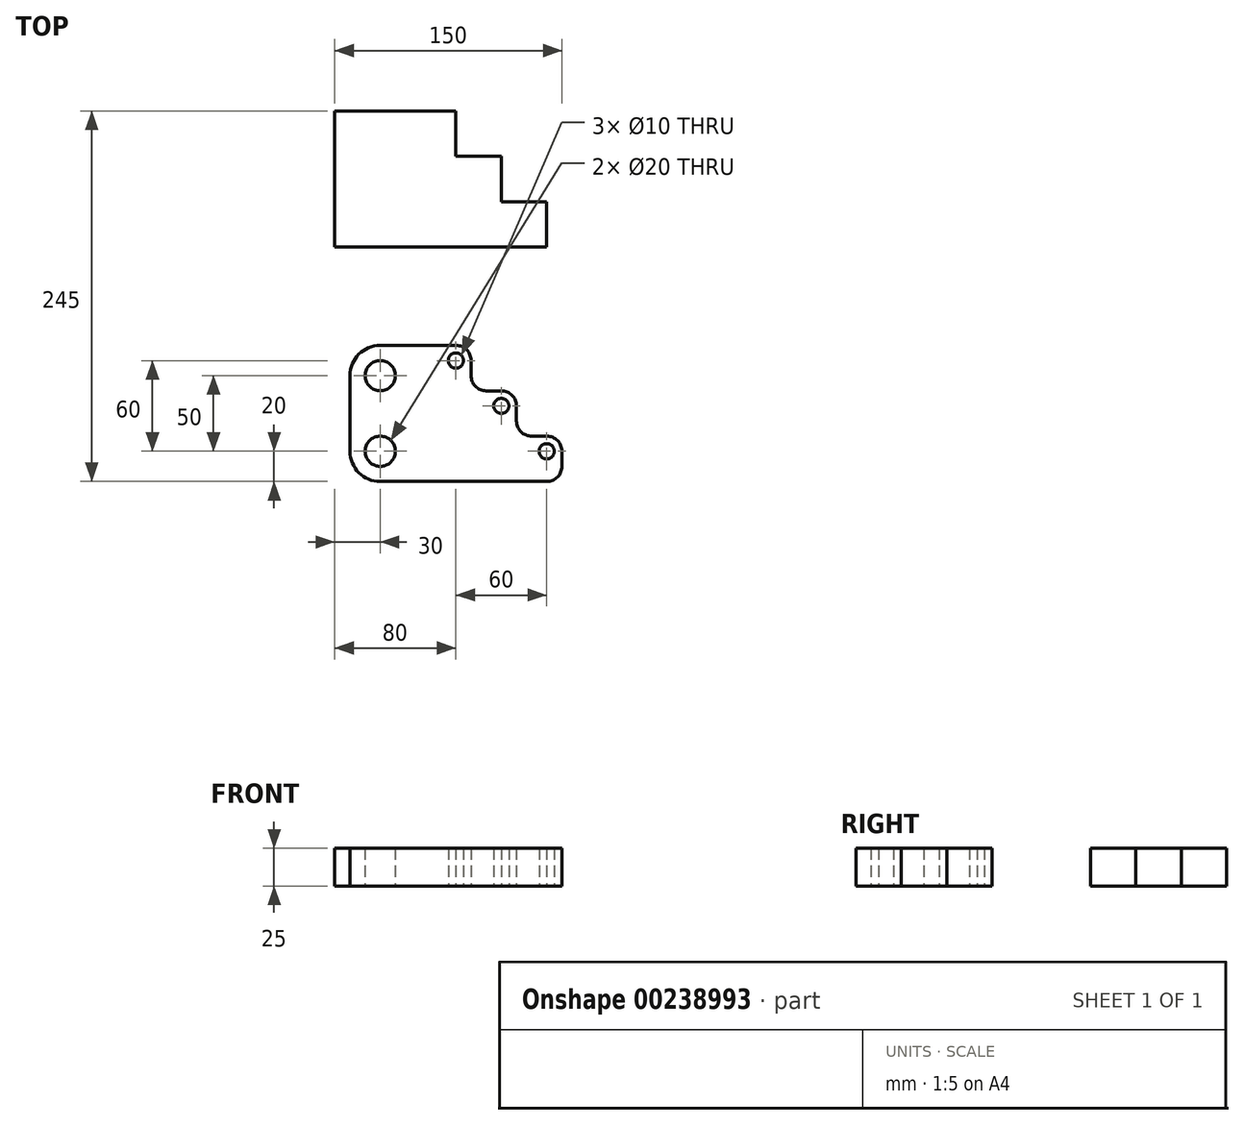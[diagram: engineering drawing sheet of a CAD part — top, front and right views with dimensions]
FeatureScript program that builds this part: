
annotation { "Feature Type Name" : "Feature", "Feature Type Description" : "" }
export const myFeature = defineFeature(function(context is Context, id is Id, definition is map)
    precondition{}
    {
        {
            var Q0;
            Q0=qCreatedBy(makeId("Top.planeOp"),FACE);
            var sketch = newSketch(context, id + "F0", { "sketchPlane" : qUnion([Q0])});
            skLineSegment(sketch, "E0", {"start": v(-110, 89.86) * mm, "end": v(-110, -0.14) * mm});
            skLineSegment(sketch, "E1", {"start": v(-110, 89.86) * mm, "end": v(-30, 89.86) * mm});
            skLineSegment(sketch, "E2", {"start": v(-30, 89.86) * mm, "end": v(-30, 59.86) * mm});
            skLineSegment(sketch, "E3", {"start": v(-30, 59.86) * mm, "end": v(0, 59.86) * mm});
            skLineSegment(sketch, "E4", {"start": v(0, 59.86) * mm, "end": v(0, 29.86) * mm});
            skLineSegment(sketch, "E5", {"start": v(0, 29.86) * mm, "end": v(30, 29.86) * mm});
            skLineSegment(sketch, "E6", {"start": v(30, 29.86) * mm, "end": v(30, -0.14) * mm});
            skLineSegment(sketch, "E7", {"start": v(30, -0.14) * mm, "end": v(-110, -0.14) * mm});
            skLineSegment(sketch, "E8", {"start": v(30, -155.14) * mm, "end": v(-80, -155.14) * mm});
            skLineSegment(sketch, "E9", {"start": v(-100, -135.14) * mm, "end": v(-100, -85.14) * mm});
            skLineSegment(sketch, "E10", {"start": v(-80, -65.14) * mm, "end": v(-30, -65.14) * mm});
            skLineSegment(sketch, "E11", {"start": v(-20, -75.14) * mm, "end": v(-20, -85.14) * mm});
            skLineSegment(sketch, "E12", {"start": v(-10, -95.14) * mm, "end": v(0, -95.14) * mm});
            skLineSegment(sketch, "E13", {"start": v(10, -105.14) * mm, "end": v(10, -115.14) * mm});
            skLineSegment(sketch, "E14", {"start": v(20, -125.14) * mm, "end": v(30, -125.14) * mm});
            skLineSegment(sketch, "E15", {"start": v(40, -135.14) * mm, "end": v(40, -145.14) * mm});
            skPoint(sketch, "E16.visualSharp", {"position": v(-100, -65.14) * mm});
            skArc(sketch, "E16.filletArc", {"start": v(-80, -65.14) * mm, "mid": v(-94.14, -71) * mm, "end": v(-100, -85.14) * mm});
            skPoint(sketch, "E17.visualSharp", {"position": v(-100, -155.14) * mm});
            skArc(sketch, "E17.filletArc", {"start": v(-100, -135.14) * mm, "mid": v(-94.14, -149.28) * mm, "end": v(-80, -155.14) * mm});
            skPoint(sketch, "E18.visualSharp", {"position": v(-20, -65.14) * mm});
            skArc(sketch, "E18.filletArc", {"start": v(-20, -75.14) * mm, "mid": v(-22.93, -68.07) * mm, "end": v(-30, -65.14) * mm});
            skArc(sketch, "E19.filletArc", {"start": v(-20, -85.14) * mm, "mid": v(-17.07, -92.21) * mm, "end": v(-10, -95.14) * mm});
            skPoint(sketch, "E20.visualSharp", {"position": v(10, -95.14) * mm});
            skArc(sketch, "E20.filletArc", {"start": v(10, -105.14) * mm, "mid": v(7.07, -98.07) * mm, "end": v(0, -95.14) * mm});
            skPoint(sketch, "E21.visualSharp", {"position": v(10, -125.14) * mm});
            skArc(sketch, "E21.filletArc", {"start": v(10, -115.14) * mm, "mid": v(12.93, -122.21) * mm, "end": v(20, -125.14) * mm});
            skPoint(sketch, "E22.visualSharp", {"position": v(40, -125.14) * mm});
            skArc(sketch, "E22.filletArc", {"start": v(40, -135.14) * mm, "mid": v(37.07, -128.07) * mm, "end": v(30, -125.14) * mm});
            skPoint(sketch, "E23.visualSharp", {"position": v(40, -155.14) * mm});
            skArc(sketch, "E23.filletArc", {"start": v(30, -155.14) * mm, "mid": v(37.07, -152.21) * mm, "end": v(40, -145.14) * mm});
            skCircle(sketch, "E24", {"center": v(-80, -135.14) * mm, "radius": 10 * mm});
            skCircle(sketch, "E25", {"center": v(-80, -85.14) * mm, "radius": 10 * mm});
            skCircle(sketch, "E26", {"center": v(-30, -75.14) * mm, "radius": 5 * mm});
            skCircle(sketch, "E27", {"center": v(0, -105.14) * mm, "radius": 5 * mm});
            skCircle(sketch, "E28", {"center": v(30, -135.14) * mm, "radius": 5 * mm});
            skPoint(sketch, "E28.perimeterSnap0", {"position": v(25, -125.14) * mm});
            skPoint(sketch, "E28.perimeterSnap1", {"position": v(40, -140.14) * mm});
            skSolve(sketch);
        }
        {
            var Q0;
            Q0=makeQuery(id+"F0.imprint","IMPRINT",FACE,{"disambiguationData":[TD([[makeQuery(id+"F0.imprint","IMPRINT",EDGE,{"derivedFrom":sQuery(id+"F0.wireOp",EDGE,"E0")}),1.0]])]});
            var Q1;
            Q1=makeQuery(id+"F0.imprint","IMPRINT",FACE,{"disambiguationData":[TD([[makeQuery(id+"F0.imprint","IMPRINT",EDGE,{"derivedFrom":sQuery(id+"F0.wireOp",EDGE,"E0")}),1.0]])]});
            var Q2;
            Q2=makeQuery(id+"F0.imprint","IMPRINT",FACE,{"disambiguationData":[TD([[makeQuery(id+"F0.imprint","IMPRINT",EDGE,{"derivedFrom":sQuery(id+"F0.wireOp",EDGE,"E8")}),-1.0]])]});
            extrude(context, id + "F1", {"entities" : qUnion([Q0, Q1, Q2]), "depth" : 25 * mm});
        }
    });
